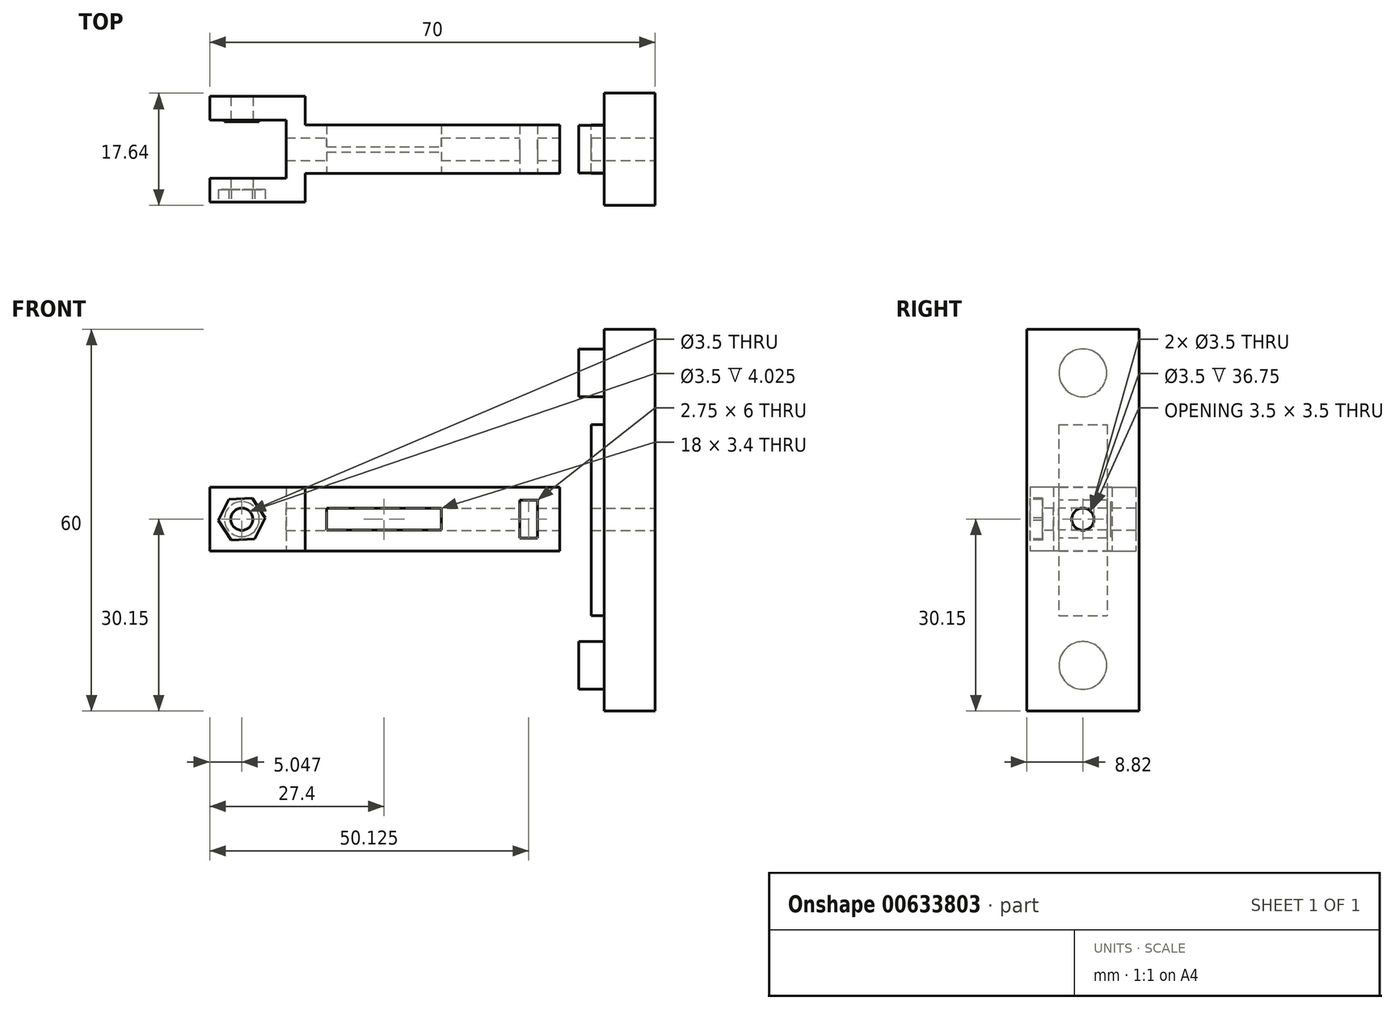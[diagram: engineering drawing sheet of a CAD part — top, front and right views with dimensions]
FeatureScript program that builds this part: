
annotation { "Feature Type Name" : "Feature", "Feature Type Description" : "" }
export const myFeature = defineFeature(function(context is Context, id is Id, definition is map)
    precondition{}
    {
        {
            var Q0;
            Q0=qCreatedBy(makeId("Top.planeOp"),FACE);
            var sketch = newSketch(context, id + "F0", { "sketchPlane" : qUnion([Q0])});
            skLineSegment(sketch, "E0.bottom", {"start": v(0, 0) * mm, "end": v(40, 0) * mm});
            skLineSegment(sketch, "E0.top", {"start": v(0, -3.83) * mm, "end": v(40, -3.83) * mm});
            skLineSegment(sketch, "E0.left", {"start": v(0, 0) * mm, "end": v(0, -3.83) * mm});
            skLineSegment(sketch, "E0.right", {"start": v(40, 0) * mm, "end": v(40, -3.83) * mm});
            skLineSegment(sketch, "E1.bottom", {"start": v(-3, 0) * mm, "end": v(0, 0) * mm});
            skLineSegment(sketch, "E1.top", {"start": v(-15, -8.32) * mm, "end": v(0, -8.32) * mm});
            skLineSegment(sketch, "E1.left", {"start": v(-15, -4.6) * mm, "end": v(-15, -8.32) * mm});
            skLineSegment(sketch, "E1.right", {"start": v(0, 0) * mm, "end": v(0, -8.32) * mm});
            skLineSegment(sketch, "E2.top", {"start": v(-15, -4.6) * mm, "end": v(-3, -4.6) * mm});
            skLineSegment(sketch, "E2.right", {"start": v(-3, 0) * mm, "end": v(-3, -4.6) * mm});
            skLineSegment(sketch, "E3.MirrorCS", {"start": v(0, 0) * mm, "end": v(0, 3.83) * mm});
            skLineSegment(sketch, "E4.MirrorCS", {"start": v(0, 0) * mm, "end": v(0, 8.32) * mm});
            skLineSegment(sketch, "E5.MirrorCS", {"start": v(-15, 4.6) * mm, "end": v(-15, 8.32) * mm});
            skLineSegment(sketch, "E6.MirrorCS", {"start": v(-3, 0) * mm, "end": v(-3, 4.6) * mm});
            skLineSegment(sketch, "E7.MirrorCS", {"start": v(-15, 8.32) * mm, "end": v(0, 8.32) * mm});
            skLineSegment(sketch, "E8.MirrorCS", {"start": v(-15, 4.6) * mm, "end": v(-3, 4.6) * mm});
            skLineSegment(sketch, "E9.MirrorCS", {"start": v(40, 0) * mm, "end": v(40, 3.83) * mm});
            skLineSegment(sketch, "E10.MirrorCS", {"start": v(0, 3.83) * mm, "end": v(40, 3.83) * mm});
            skSolve(sketch);
        }
        {
            var Q0;
            {var subQ2=sQuery(id+"F0.wireOp",EDGE,"E1.top");Q0=makeQuery(id+"F0.imprint","IMPRINT",FACE,{"disambiguationData":[TD([[makeQuery(id+"F0.imprint","IMPRINT",EDGE,{"derivedFrom":subQ2}),1.0]])]});}
            var Q1;
            Q1=makeQuery(id+"F0.imprint","IMPRINT",FACE,{"disambiguationData":[TD([[makeQuery(id+"F0.imprint","IMPRINT",EDGE,{"derivedFrom":sQuery(id+"F0.wireOp",EDGE,"E5.MirrorCS")}),-1.0]])]});
            var Q2;
            {var subQ0=sQuery(id+"F0.wireOp",EDGE,"E0.bottom");Q2=makeQuery(id+"F0.imprint","IMPRINT",FACE,{"disambiguationData":[TD([[makeQuery(id+"F0.imprint","IMPRINT",EDGE,{"derivedFrom":subQ0}),1.0]])]});}
            var Q3;
            {var subQ0=sQuery(id+"F0.wireOp",EDGE,"E0.bottom");Q3=makeQuery(id+"F0.imprint","IMPRINT",FACE,{"disambiguationData":[TD([[makeQuery(id+"F0.imprint","IMPRINT",EDGE,{"derivedFrom":subQ0}),-1.0]])]});}
            extrude(context, id + "F1", {"entities" : qUnion([Q0, Q1, Q2, Q3]), "depth" : 10 * mm});
        }
        {
            var Q0;
            Q0=makeQuery(id+"F1.opExtrude","SWEPT_FACE",FACE,{"disambiguationData":[OSD([sQuery(id+"F0.wireOp",EDGE,"E1.top")])]});
            var sketch = newSketch(context, id + "F2", { "sketchPlane" : qUnion([Q0])});
            skCircle(sketch, "E11", {"center": v(-9.95, 5) * mm, "radius": 1.75 * mm});
            skSolve(sketch);
        }
        {
            var Q0;
            Q0=makeQuery(id+"F2.imprint","IMPRINT",FACE,{"disambiguationData":[TD([[makeQuery(id+"F2.imprint","IMPRINT",EDGE,{"derivedFrom":sQuery(id+"F2.wireOp",EDGE,"E11")}),1.0]])]});
            extrude(context, id + "F3", {"entities" : qUnion([Q0]), "operationType" : NewBodyOperationType.REMOVE, "endBound" : BoundingType.THROUGH_ALL, "oppositeDirection" : true, "depth" : 25 * mm});
        }
        {
            var Q0;
            Q0=makeQuery(id+"F1.opExtrude","SWEPT_FACE",FACE,{"disambiguationData":[OSD([sQuery(id+"F0.wireOp",EDGE,"E0.top")])]});
            var sketch = newSketch(context, id + "F4", { "sketchPlane" : qUnion([Q0])});
            skLineSegment(sketch, "E12.bottom", {"start": v(3.4, 3.3) * mm, "end": v(21.4, 3.3) * mm});
            skLineSegment(sketch, "E12.top", {"start": v(3.4, 6.7) * mm, "end": v(21.4, 6.7) * mm});
            skLineSegment(sketch, "E12.left", {"start": v(3.4, 3.3) * mm, "end": v(3.4, 6.7) * mm});
            skLineSegment(sketch, "E12.right", {"start": v(21.4, 3.3) * mm, "end": v(21.4, 6.7) * mm});
            skLineSegment(sketch, "E13.bottom", {"start": v(33.75, 8) * mm, "end": v(36.5, 8) * mm});
            skLineSegment(sketch, "E13.top", {"start": v(33.75, 2) * mm, "end": v(36.5, 2) * mm});
            skLineSegment(sketch, "E13.left", {"start": v(33.75, 8) * mm, "end": v(33.75, 2) * mm});
            skLineSegment(sketch, "E13.right", {"start": v(36.5, 8) * mm, "end": v(36.5, 2) * mm});
            skSolve(sketch);
        }
        {
            var Q0;
            Q0=makeQuery(id+"F4.imprint","IMPRINT",FACE,{"disambiguationData":[TD([[makeQuery(id+"F4.imprint","IMPRINT",EDGE,{"derivedFrom":sQuery(id+"F4.wireOp",EDGE,"E12.bottom")}),1.0]])]});
            var Q1;
            Q1=makeQuery(id+"F4.imprint","IMPRINT",FACE,{"disambiguationData":[TD([[makeQuery(id+"F4.imprint","IMPRINT",EDGE,{"derivedFrom":sQuery(id+"F4.wireOp",EDGE,"E13.bottom")}),-1.0]])]});
            extrude(context, id + "F5", {"entities" : qUnion([Q0, Q1]), "operationType" : NewBodyOperationType.REMOVE, "endBound" : BoundingType.THROUGH_ALL, "oppositeDirection" : true, "depth" : 25 * mm});
        }
        {
            var Q0;
            Q0=makeQuery(id+"F1.opExtrude","SWEPT_FACE",FACE,{"disambiguationData":[OSD([sQuery(id+"F0.wireOp",EDGE,"E0.right"),sQuery(id+"F0.wireOp",EDGE,"E9.MirrorCS")])]});
            var sketch = newSketch(context, id + "F6", { "sketchPlane" : qUnion([Q0])});
            skCircle(sketch, "E14", {"center": v(0, 5) * mm, "radius": 1.75 * mm});
            skSolve(sketch);
        }
        {
            var Q0;
            Q0=makeQuery(id+"F6.imprint","IMPRINT",FACE,{"disambiguationData":[TD([[makeQuery(id+"F6.imprint","IMPRINT",EDGE,{"derivedFrom":sQuery(id+"F6.wireOp",EDGE,"E14")}),1.0]])]});
            extrude(context, id + "F7", {"entities" : qUnion([Q0]), "operationType" : NewBodyOperationType.REMOVE, "oppositeDirection" : true, "depth" : 15 * mm});
        }
        {
            var Q0;
            Q0=makeQuery(id+"F1.opExtrude","SWEPT_FACE",FACE,{"disambiguationData":[OSD([sQuery(id+"F0.wireOp",EDGE,"E0.right"),sQuery(id+"F0.wireOp",EDGE,"E9.MirrorCS")])]});
            cPlane(context, id + "F8", {"entities" : qUnion([Q0]), "cplaneType" : CPlaneType.OFFSET, "offset" : 5 * mm, "width" : 150 * mm, "height" : 150 * mm});
        }
        {
            var Q0;
            Q0=qCreatedBy(id+"F8.planeOp",FACE);
            var sketch = newSketch(context, id + "F9", { "sketchPlane" : qUnion([Q0])});
            skLineSegment(sketch, "E15.0", {"start": v(3.83, 10) * mm, "end": v(3.83, 0) * mm});
            skLineSegment(sketch, "E16.0", {"start": v(-3.82, 10) * mm, "end": v(-3.82, 0) * mm});
            skLineSegment(sketch, "E17.bottom", {"start": v(-3.82, 19.85) * mm, "end": v(3.83, 19.85) * mm});
            skLineSegment(sketch, "E17.top", {"start": v(-3.82, -10.15) * mm, "end": v(3.83, -10.15) * mm});
            skLineSegment(sketch, "E17.left", {"start": v(-3.82, 19.85) * mm, "end": v(-3.82, -10.15) * mm});
            skLineSegment(sketch, "E17.right", {"start": v(3.83, 19.85) * mm, "end": v(3.83, -10.15) * mm});
            skPoint(sketch, "E18.oppositeSnap0", {"position": v(3.83, 4.85) * mm});
            skLineSegment(sketch, "E18.bottom", {"start": v(3.83, 4.85) * mm, "end": v(3.83, 4.85) * mm});
            skLineSegment(sketch, "E18.top", {"start": v(3.83, 4.85) * mm, "end": v(3.83, 4.85) * mm});
            skLineSegment(sketch, "E18.left", {"start": v(3.83, 4.85) * mm, "end": v(3.83, 4.85) * mm});
            skLineSegment(sketch, "E18.right", {"start": v(3.83, 4.85) * mm, "end": v(3.83, 4.85) * mm});
            skSolve(sketch);
        }
        {
            var Q0;
            {var subQ0=sQuery(id+"F9.wireOp",EDGE,"E17.bottom");Q0=makeQuery(id+"F9.imprint","IMPRINT",FACE,{"disambiguationData":[TD([[makeQuery(id+"F9.imprint","IMPRINT",EDGE,{"derivedFrom":subQ0}),-1.0]])]});}
            extrude(context, id + "F10", {"entities" : qUnion([Q0]), "depth" : 2 * mm});
        }
        {
            var Q0;
            Q0=makeQuery(id+"F10.opExtrude","CAP_FACE",FACE,{"disambiguationData":[OSD([sQuery(id+"F9.wireOp",EDGE,"E17.bottom"),sQuery(id+"F9.wireOp",EDGE,"E17.top"),sQuery(id+"F9.wireOp",EDGE,"E17.left"),sQuery(id+"F9.wireOp",EDGE,"E17.right")])],"isStart":false});
            var sketch = newSketch(context, id + "F11", { "sketchPlane" : qUnion([Q0])});
            skLineSegment(sketch, "E19.bottom", {"start": v(8.82, 34.85) * mm, "end": v(-8.83, 34.85) * mm});
            skLineSegment(sketch, "E19.top", {"start": v(8.83, -25.15) * mm, "end": v(-8.82, -25.15) * mm});
            skLineSegment(sketch, "E19.left", {"start": v(8.82, 34.85) * mm, "end": v(8.83, -25.15) * mm});
            skLineSegment(sketch, "E19.right", {"start": v(-8.83, 34.85) * mm, "end": v(-8.82, -25.15) * mm});
            skSolve(sketch);
        }
        {
            var Q0;
            Q0=qSketchRegion(id+"F11",true);
            extrude(context, id + "F12", {"entities" : qUnion([Q0]), "operationType" : NewBodyOperationType.ADD, "depth" : 8 * mm});
        }
        {
            var Q0;
            Q0=makeQuery(id+"F12.opExtrude","CAP_FACE",FACE,{"disambiguationData":[OSD([sQuery(id+"F11.wireOp",EDGE,"E19.bottom"),sQuery(id+"F11.wireOp",EDGE,"E19.top"),sQuery(id+"F11.wireOp",EDGE,"E19.left"),sQuery(id+"F11.wireOp",EDGE,"E19.right")])],"isStart":false});
            var sketch = newSketch(context, id + "F13", { "sketchPlane" : qUnion([Q0])});
            skCircle(sketch, "E20.0", {"center": v(0, 5) * mm, "radius": 1.75 * mm});
            skSolve(sketch);
        }
        {
            var Q0;
            Q0=makeQuery(id+"F13.imprint","IMPRINT",FACE,{"disambiguationData":[TD([[makeQuery(id+"F13.imprint","IMPRINT",EDGE,{"derivedFrom":sQuery(id+"F13.wireOp",EDGE,"E20.0")}),1.0]])]});
            extrude(context, id + "F14", {"entities" : qUnion([Q0]), "operationType" : NewBodyOperationType.REMOVE, "endBound" : BoundingType.THROUGH_ALL, "oppositeDirection" : true, "depth" : 25 * mm});
        }
        {
            var Q0;
            Q0=makeQuery(id+"F1.opExtrude","SWEPT_FACE",FACE,{"disambiguationData":[OSD([sQuery(id+"F0.wireOp",EDGE,"E8.MirrorCS")])]});
            var sketch = newSketch(context, id + "F15", { "sketchPlane" : qUnion([Q0])});
            skCircle(sketch, "E21", {"center": v(-9.95, 5) * mm, "radius": 1.75 * mm});
            skCircle(sketch, "E22", {"center": v(-9.95, 5) * mm, "radius": 2.75 * mm});
            skSolve(sketch);
        }
        {
            var Q0;
            Q0=makeQuery(id+"F15.imprint","IMPRINT",FACE,{"disambiguationData":[TD([[makeQuery(id+"F15.imprint","IMPRINT",EDGE,{"derivedFrom":sQuery(id+"F15.wireOp",EDGE,"E21")}),1.0]])]});
            extrude(context, id + "F16", {"entities" : qUnion([Q0]), "operationType" : NewBodyOperationType.ADD, "depth" : 0.3 * mm});
        }
        {
            var Q0;
            Q0=makeQuery(id+"F1.opExtrude","SWEPT_FACE",FACE,{"disambiguationData":[OSD([sQuery(id+"F0.wireOp",EDGE,"E1.top")])]});
            var sketch = newSketch(context, id + "F17", { "sketchPlane" : qUnion([Q0])});
            skCircle(sketch, "E23.cCircle", {"center": v(-9.95, 5) * mm, "radius": 3.2 * mm, "construction": true});
            skLineSegment(sketch, "E23.0", {"start": v(-6.26, 5.2) * mm, "end": v(-7.93, 1.9) * mm});
            skLineSegment(sketch, "E23.1", {"start": v(-7.93, 1.9) * mm, "end": v(-11.62, 1.7) * mm});
            skLineSegment(sketch, "E23.2", {"start": v(-11.62, 1.7) * mm, "end": v(-13.64, 4.8) * mm});
            skLineSegment(sketch, "E23.3", {"start": v(-13.64, 4.8) * mm, "end": v(-11.98, 8.1) * mm});
            skLineSegment(sketch, "E23.4", {"start": v(-11.98, 8.1) * mm, "end": v(-8.29, 8.3) * mm});
            skLineSegment(sketch, "E23.5", {"start": v(-8.29, 8.3) * mm, "end": v(-6.26, 5.2) * mm});
            skPoint(sketch, "E23.0.midPoint", {"position": v(-7.1, 3.56) * mm});
            skSolve(sketch);
        }
        {
            var Q0;
            Q0=makeQuery(id+"F17.imprint","IMPRINT",FACE,{"disambiguationData":[TD([[makeQuery(id+"F17.imprint","IMPRINT",EDGE,{"derivedFrom":sQuery(id+"F17.wireOp",EDGE,"E23.0")}),-1.0]])]});
            extrude(context, id + "F18", {"entities" : qUnion([Q0]), "operationType" : NewBodyOperationType.REMOVE, "oppositeDirection" : true, "depth" : 2 * mm});
        }
        {
            var Q0;
            Q0=makeQuery(id+"F12.opExtrude","CAP_FACE",FACE,{"disambiguationData":[OSD([sQuery(id+"F11.wireOp",EDGE,"E19.bottom"),sQuery(id+"F11.wireOp",EDGE,"E19.top"),sQuery(id+"F11.wireOp",EDGE,"E19.left"),sQuery(id+"F11.wireOp",EDGE,"E19.right")])],"isStart":true});
            var sketch = newSketch(context, id + "F19", { "sketchPlane" : qUnion([Q0])});
            skCircle(sketch, "E24.0", {"center": v(0, 5) * mm, "radius": 1.75 * mm});
            skCircle(sketch, "E25", {"center": v(0, -18) * mm, "radius": 3.75 * mm});
            skCircle(sketch, "E26", {"center": v(0, 28) * mm, "radius": 3.75 * mm});
            skSolve(sketch);
        }
        {
            var Q0;
            Q0=makeQuery(id+"F19.imprint","IMPRINT",FACE,{"disambiguationData":[TD([[makeQuery(id+"F19.imprint","IMPRINT",EDGE,{"derivedFrom":sQuery(id+"F19.wireOp",EDGE,"E26")}),1.0]])]});
            var Q1;
            Q1=makeQuery(id+"F19.imprint","IMPRINT",FACE,{"disambiguationData":[TD([[makeQuery(id+"F19.imprint","IMPRINT",EDGE,{"derivedFrom":sQuery(id+"F19.wireOp",EDGE,"E25")}),1.0]])]});
            extrude(context, id + "F20", {"entities" : qUnion([Q0, Q1]), "operationType" : NewBodyOperationType.ADD, "depth" : 4 * mm});
        }
    });
